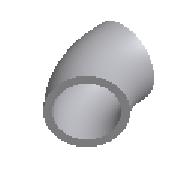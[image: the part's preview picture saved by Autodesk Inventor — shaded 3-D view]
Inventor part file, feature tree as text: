
AUTODESK INVENTOR PART (.ipt)
format: ipt  version: 2023.1 (Build 271208000, 208)  size: 179,200 bytes
history: native  units: mm (DEFAULTED — no unit token found)
features: other x4, sketch x2, sweep x1
ambient origin geometry x8: Origin, YZ Plane, XZ Plane, XY Plane, X Axis, Y Axis, Z Axis, Center Point
bodies: Solid1 (feature_tree)
feature tree (7):
  sweep  "Sweep1"
  other  "Work Point1"
  other  "Work Point2"
  other  "Work Axis1"
  other  "Work Axis2"
  sketch  "Sketch1"  dims[d0=93.2mm d1=101.6mm]
  sketch  "Sketch2"  dims[d2=36.8mm d3=45.0deg d4=36.8mm d5=0.0mm d6=0.0mm]
